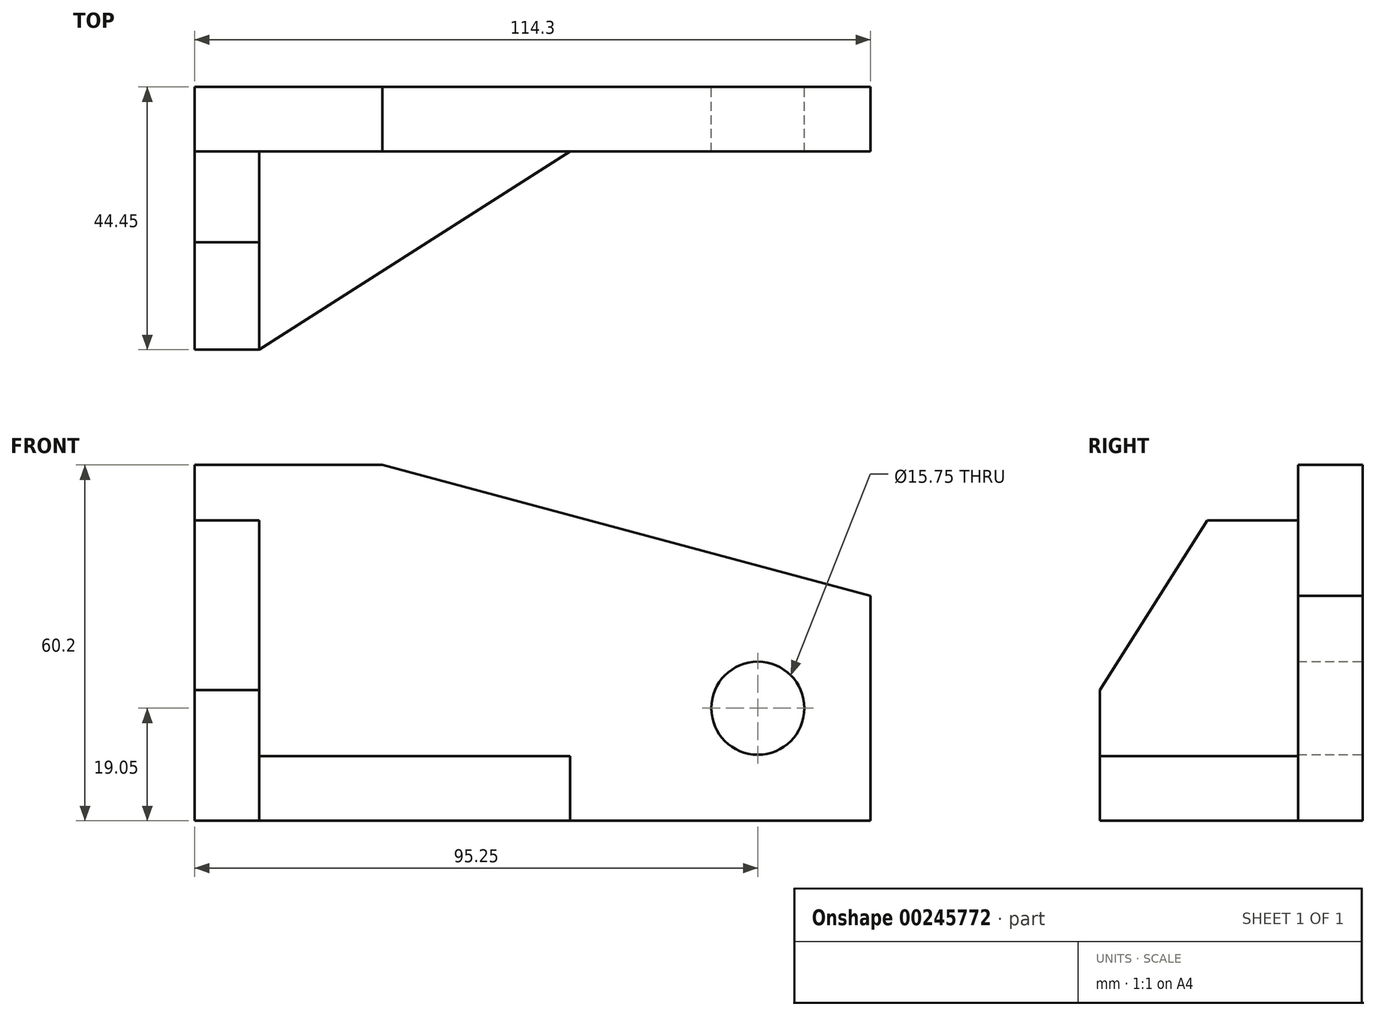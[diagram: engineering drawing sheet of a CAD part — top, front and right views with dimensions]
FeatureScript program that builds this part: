
annotation { "Feature Type Name" : "Feature", "Feature Type Description" : "" }
export const myFeature = defineFeature(function(context is Context, id is Id, definition is map)
    precondition{}
    {
        {
            var Q0;
            Q0=qCreatedBy(makeId("Front.planeOp"),FACE);
            var sketch = newSketch(context, id + "F0", { "sketchPlane" : qUnion([Q0])});
            skLineSegment(sketch, "E0", {"start": v(0, 0) * mm, "end": v(0, 60.2) * mm});
            skLineSegment(sketch, "E1", {"start": v(0, 60.2) * mm, "end": v(31.75, 60.2) * mm});
            skLineSegment(sketch, "E2", {"start": v(114.3, 38.08) * mm, "end": v(114.3, 0) * mm});
            skLineSegment(sketch, "E3", {"start": v(114.3, 0) * mm, "end": v(0, 0) * mm});
            skPoint(sketch, "E4", {"position": v(31.75, 60.2) * mm});
            skLineSegment(sketch, "E5", {"start": v(31.75, 60.2) * mm, "end": v(114.3, 38.08) * mm});
            skPoint(sketch, "E6", {"position": v(95.25, 19.05) * mm});
            skCircle(sketch, "E7", {"center": v(95.25, 19.05) * mm, "radius": 7.87 * mm});
            skSolve(sketch);
        }
        {
            var Q0;
            Q0=makeQuery(id+"F0.imprint","IMPRINT",FACE,{"disambiguationData":[TD([[makeQuery(id+"F0.imprint","IMPRINT",EDGE,{"derivedFrom":sQuery(id+"F0.wireOp",EDGE,"E0")}),-1.0]])]});
            extrude(context, id + "F1", {"entities" : qUnion([Q0]), "depth" : 10.92 * mm});
        }
        {
            var Q0;
            Q0=qCreatedBy(makeId("Right.planeOp"),FACE);
            var sketch = newSketch(context, id + "F2", { "sketchPlane" : qUnion([Q0])});
            skLineSegment(sketch, "E8", {"start": v(0, 0) * mm, "end": v(-44.45, 0) * mm});
            skLineSegment(sketch, "E9", {"start": v(-44.45, 0) * mm, "end": v(-44.45, 22.1) * mm});
            skLineSegment(sketch, "E10", {"start": v(-26.27, 50.8) * mm, "end": v(-10.92, 50.8) * mm});
            skLineSegment(sketch, "E11", {"start": v(-10.92, 50.8) * mm, "end": v(-10.92, 0) * mm});
            skLineSegment(sketch, "E12", {"start": v(-44.45, 22.1) * mm, "end": v(-26.27, 50.8) * mm});
            skPoint(sketch, "E13", {"position": v(-10.92, 0) * mm});
            skPoint(sketch, "E14", {"position": v(-44.45, 0) * mm});
            skSolve(sketch);
        }
        {
            var Q0;
            {var subQ1=sQuery(id+"F2.wireOp",EDGE,"E9");Q0=makeQuery(id+"F2.imprint","IMPRINT",FACE,{"disambiguationData":[TD([[makeQuery(id+"F2.imprint","IMPRINT",EDGE,{"derivedFrom":subQ1}),-1.0]])]});}
            extrude(context, id + "F3", {"entities" : qUnion([Q0]), "operationType" : NewBodyOperationType.ADD, "depth" : 10.92 * mm});
        }
        {
            var Q0;
            Q0=qCreatedBy(makeId("Top.planeOp"),FACE);
            var sketch = newSketch(context, id + "F4", { "sketchPlane" : qUnion([Q0])});
            skPoint(sketch, "E15", {"position": v(10.92, -44.45) * mm});
            skPoint(sketch, "E16", {"position": v(63.5, -10.92) * mm});
            skPoint(sketch, "E17.left.end.orphan", {"position": v(0, -44.45) * mm});
            skPoint(sketch, "E18.orphan", {"position": v(63.5, 0) * mm});
            skLineSegment(sketch, "E19", {"start": v(10.92, -44.45) * mm, "end": v(63.5, -10.92) * mm});
            skPoint(sketch, "E20.end.orphan", {"position": v(10.92, -10.92) * mm});
            skLineSegment(sketch, "E21", {"start": v(10.92, -44.45) * mm, "end": v(10.92, -10.92) * mm});
            skLineSegment(sketch, "E22", {"start": v(63.5, -10.92) * mm, "end": v(10.92, -10.92) * mm});
            skSolve(sketch);
        }
        {
            var Q0;
            Q0=makeQuery(id+"F4.imprint","IMPRINT",FACE,{"disambiguationData":[TD([[makeQuery(id+"F4.imprint","IMPRINT",EDGE,{"derivedFrom":sQuery(id+"F4.wireOp",EDGE,"E19")}),1.0]])]});
            extrude(context, id + "F5", {"entities" : qUnion([Q0]), "operationType" : NewBodyOperationType.ADD, "depth" : 10.92 * mm});
        }
    });
